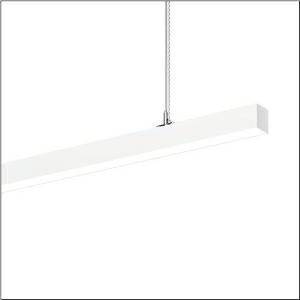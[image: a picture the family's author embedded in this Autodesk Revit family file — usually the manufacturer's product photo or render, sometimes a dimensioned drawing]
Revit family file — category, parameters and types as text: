
# Revit family: silica_r__21_51mx30da44wb_0345
name_source: partatom
category: Lighting Fixtures
units: mm (PartAtom-declared; Revit-internal decimal feet)

## family parameters
Cut with Voids When Loaded = No
Host = Face
Light Source = No
Part Type = Normal
Room Calculation Point = No
Round Connector Dimension = Use Diameter
Shared = No

## types (1)
- --- (1 x LED, 4210 lm, 26 W, 4000K)
    Apparent Load = 26 VA
    CIE Flux Codes = 47 79 96 57 100
    Color Rendering = 80
    Color Temperature = 4000K
    Default Elevation = 1800 mm
    Description = Silica® 21, office luminaire, primary optical cover: cover, of PMMA, opal, light emission: direct/indirect distribution, primary light characteristic: symmetric, installation type: suspended mounting, LED, rated luminous flux: 4.210lm, luminous efficacy: 162lm/W, light colour: 840, colour temperature: 4000K, control gear: DALI 2, with terminal, 3+2-pole, max. 2.5mm², mains connection: 220..240V, AC, 50/60Hz, rated input power: 26W, luminaire housing, of aluminium, traffic white (RAL 9016), length: 1.204mm, width: 53mm, height: 53mm, protection rating (complete): IP20, insulation class (complete): insulation class I (protective earthing), certification: CE, permissible operating ambient temperature: 0..+35°C, standard: EN 50419, packaging unit: 1 piece
    Height = 53 mm
    Lamp = 1 x LED
    Lamp Light Flux = 4210 lm
    Lamp Power = 26 W
    Lamp count = 1
    Length = 1204 mm
    Luminous efficacy = 162 lm/W
    Manufacturer = Siteco
    ModVariant = No
    Model = 51MX30DA44WB
    Mounting Place = Ceiling
    Mounting Type = Pendant
    Number of Poles = 1
    OnlyDefault = Yes
    Power Factor = 1
    Product Name = Silica® 21
    Product group = office luminaire | ceiling pendant
    ProductGroupID = 904
    Protection Class = Protection class I
    Protection Degree = IP 20
    RLX_Detail_Level = 1
    RLX_Emergency_Light_Flux = 0 lm
    RLX_Emergency_Type = 0
    RLX_Emergency_Type_DB = No
    RlxData = <blob elided: 20609 chars, md5=8d3a57a4>
    Socket = socket
    Standby Power = 0 W
    System Light Flux = 4210 lm
    System Power = 26 W
    Type Comments = factory setting: luminous flux: 100 % | dim-lin: 254 | 218 mA
    Type Image = l_1349023.jpg
    URL = http://relux.com
    VarID = @adj_117514
    Voltage = 0 V
    Weight = 0.00 kg
    Width = 53 mm

## geometry (parser evidence)
native form markers: Blend x4, Sweep x13
no freeform markers — native parametric forms only
